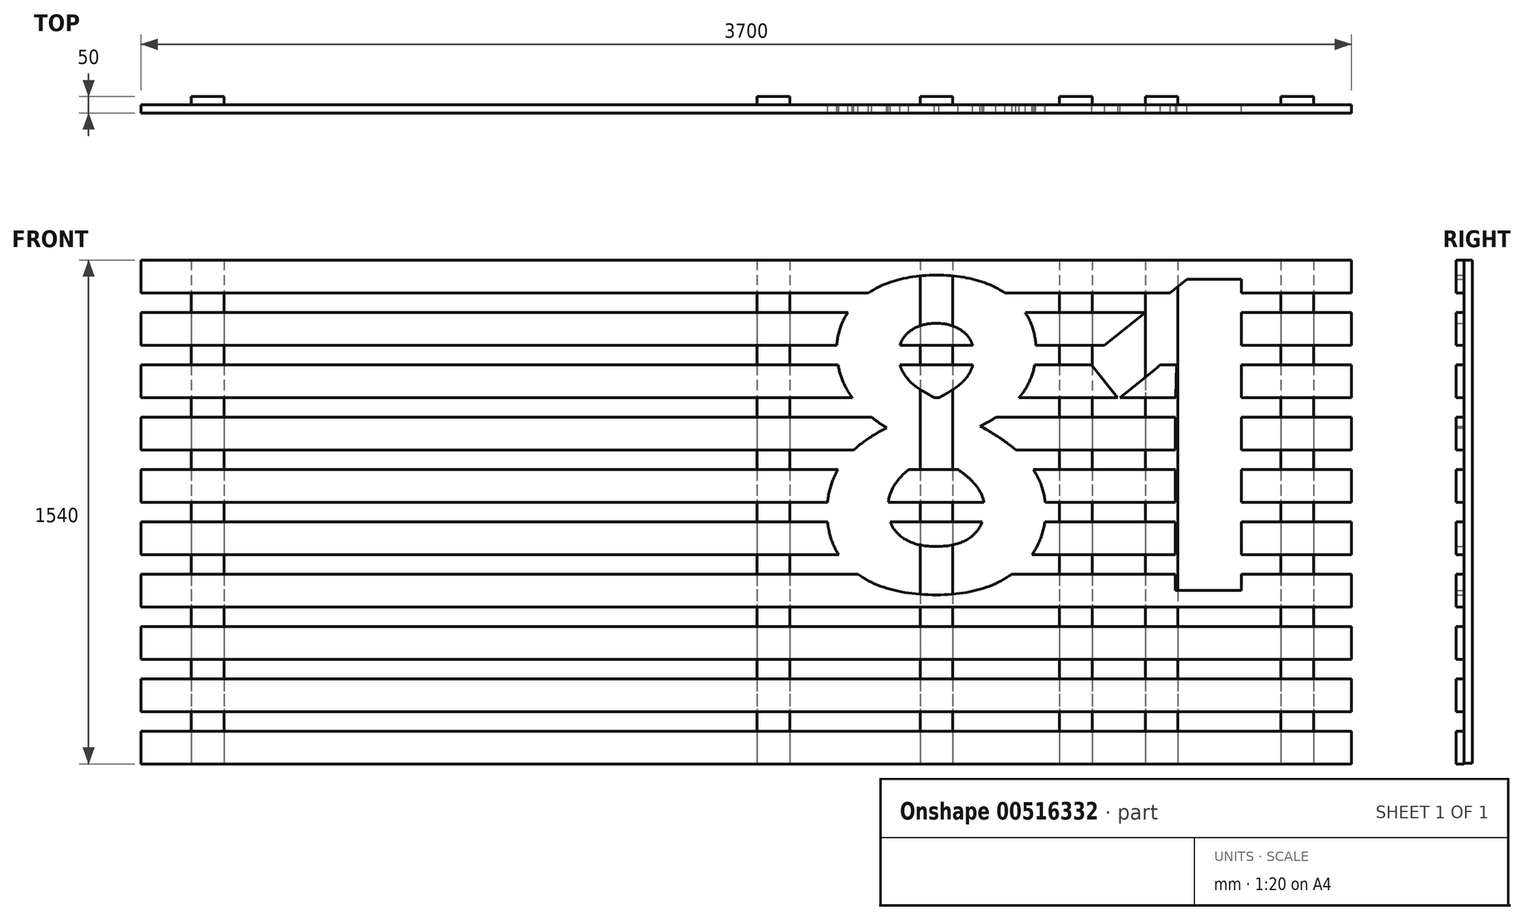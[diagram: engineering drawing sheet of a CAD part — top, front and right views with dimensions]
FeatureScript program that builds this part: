
annotation { "Feature Type Name" : "Feature", "Feature Type Description" : "" }
export const myFeature = defineFeature(function(context is Context, id is Id, definition is map)
    precondition{}
    {
        {
            var Q0;
            Q0=qCreatedBy(makeId("Front.planeOp"),FACE);
            var sketch = newSketch(context, id + "F0", { "sketchPlane" : qUnion([Q0])});
            skLineSegment(sketch, "E0.bottom", {"start": v(-1471.72, 851.39) * mm, "end": v(2278.28, 851.39) * mm, "construction": true});
            skLineSegment(sketch, "E0.top", {"start": v(-1471.72, -868.61) * mm, "end": v(2278.28, -868.61) * mm, "construction": true});
            skLineSegment(sketch, "E0.left", {"start": v(-1471.72, 851.39) * mm, "end": v(-1471.72, -868.61) * mm, "construction": true});
            skLineSegment(sketch, "E0.right", {"start": v(2278.28, 851.39) * mm, "end": v(2278.28, -868.61) * mm, "construction": true});
            skLineSegment(sketch, "E1.bottom", {"start": v(-1440.67, 798.6) * mm, "end": v(2259.33, 798.6) * mm});
            skLineSegment(sketch, "E1.top", {"start": v(-1440.67, 698.6) * mm, "end": v(2259.33, 698.6) * mm});
            skLineSegment(sketch, "E1.left", {"start": v(-1440.67, 798.6) * mm, "end": v(-1440.67, 698.6) * mm});
            skLineSegment(sketch, "E1.right", {"start": v(2259.33, 798.6) * mm, "end": v(2259.33, 698.6) * mm});
            skLineSegment(sketch, "E2.0.1.0", {"start": v(-1440.67, 538.6) * mm, "end": v(2259.33, 538.6) * mm});
            skLineSegment(sketch, "E2.0.1.1", {"start": v(-1440.67, 638.6) * mm, "end": v(2259.33, 638.6) * mm});
            skLineSegment(sketch, "E2.0.1.2", {"start": v(-1440.67, 638.6) * mm, "end": v(-1440.67, 538.6) * mm});
            skLineSegment(sketch, "E2.0.1.3", {"start": v(2259.33, 638.6) * mm, "end": v(2259.33, 538.6) * mm});
            skLineSegment(sketch, "E2.0.2.0", {"start": v(-1440.67, 378.6) * mm, "end": v(2259.33, 378.6) * mm});
            skLineSegment(sketch, "E2.0.2.1", {"start": v(-1440.67, 478.6) * mm, "end": v(2259.33, 478.6) * mm});
            skLineSegment(sketch, "E2.0.2.2", {"start": v(-1440.67, 478.6) * mm, "end": v(-1440.67, 378.6) * mm});
            skLineSegment(sketch, "E2.0.2.3", {"start": v(2259.33, 478.6) * mm, "end": v(2259.33, 378.6) * mm});
            skLineSegment(sketch, "E2.0.3.0", {"start": v(-1440.67, 218.6) * mm, "end": v(2259.33, 218.6) * mm});
            skLineSegment(sketch, "E2.0.3.1", {"start": v(-1440.67, 318.6) * mm, "end": v(2259.33, 318.6) * mm});
            skLineSegment(sketch, "E2.0.3.2", {"start": v(-1440.67, 318.6) * mm, "end": v(-1440.67, 218.6) * mm});
            skLineSegment(sketch, "E2.0.3.3", {"start": v(2259.33, 318.6) * mm, "end": v(2259.33, 218.6) * mm});
            skLineSegment(sketch, "E2.0.4.0", {"start": v(-1440.67, 58.6) * mm, "end": v(2259.33, 58.6) * mm});
            skLineSegment(sketch, "E2.0.4.1", {"start": v(-1440.67, 158.6) * mm, "end": v(2259.33, 158.6) * mm});
            skLineSegment(sketch, "E2.0.4.2", {"start": v(-1440.67, 158.6) * mm, "end": v(-1440.67, 58.6) * mm});
            skLineSegment(sketch, "E2.0.4.3", {"start": v(2259.33, 158.6) * mm, "end": v(2259.33, 58.6) * mm});
            skLineSegment(sketch, "E2.0.5.0", {"start": v(-1440.67, -101.4) * mm, "end": v(2259.33, -101.4) * mm});
            skLineSegment(sketch, "E2.0.5.1", {"start": v(-1440.67, -1.4) * mm, "end": v(2259.33, -1.4) * mm});
            skLineSegment(sketch, "E2.0.5.2", {"start": v(-1440.67, -1.4) * mm, "end": v(-1440.67, -101.4) * mm});
            skLineSegment(sketch, "E2.0.5.3", {"start": v(2259.33, -1.4) * mm, "end": v(2259.33, -101.4) * mm});
            skLineSegment(sketch, "E2.0.6.0", {"start": v(-1440.67, -261.4) * mm, "end": v(2259.33, -261.4) * mm});
            skLineSegment(sketch, "E2.0.6.1", {"start": v(-1440.67, -161.4) * mm, "end": v(2259.33, -161.4) * mm});
            skLineSegment(sketch, "E2.0.6.2", {"start": v(-1440.67, -161.4) * mm, "end": v(-1440.67, -261.4) * mm});
            skLineSegment(sketch, "E2.0.6.3", {"start": v(2259.33, -161.4) * mm, "end": v(2259.33, -261.4) * mm});
            skLineSegment(sketch, "E2.0.7.0", {"start": v(-1440.67, -421.4) * mm, "end": v(2259.33, -421.4) * mm});
            skLineSegment(sketch, "E2.0.7.1", {"start": v(-1440.67, -321.4) * mm, "end": v(2259.33, -321.4) * mm});
            skLineSegment(sketch, "E2.0.7.2", {"start": v(-1440.67, -321.4) * mm, "end": v(-1440.67, -421.4) * mm});
            skLineSegment(sketch, "E2.0.7.3", {"start": v(2259.33, -321.4) * mm, "end": v(2259.33, -421.4) * mm});
            skLineSegment(sketch, "E2.direction1", {"start": v(-1440.67, 698.6) * mm, "end": v(-2006.52, 698.6) * mm, "construction": true});
            skLineSegment(sketch, "E2.direction2", {"start": v(-1440.67, 698.6) * mm, "end": v(-1440.67, 538.6) * mm, "construction": true});
            skLineSegment(sketch, "E3.0.0.8", {"start": v(-1440.67, -581.4) * mm, "end": v(2259.33, -581.4) * mm});
            skLineSegment(sketch, "E3.3.0.8", {"start": v(-1440.67, -481.4) * mm, "end": v(2259.33, -481.4) * mm});
            skLineSegment(sketch, "E3.6.0.8", {"start": v(-1440.67, -481.4) * mm, "end": v(-1440.67, -581.4) * mm});
            skLineSegment(sketch, "E3.9.0.8", {"start": v(2259.33, -481.4) * mm, "end": v(2259.33, -581.4) * mm});
            skLineSegment(sketch, "E3.0.0.9", {"start": v(-1440.67, -741.4) * mm, "end": v(2259.33, -741.4) * mm});
            skLineSegment(sketch, "E3.3.0.9", {"start": v(-1440.67, -641.4) * mm, "end": v(2259.33, -641.4) * mm});
            skLineSegment(sketch, "E3.6.0.9", {"start": v(-1440.67, -641.4) * mm, "end": v(-1440.67, -741.4) * mm});
            skLineSegment(sketch, "E3.9.0.9", {"start": v(2259.33, -641.4) * mm, "end": v(2259.33, -741.4) * mm});
            skSolve(sketch);
        }
        {
            var Q0;
            Q0 = qSketchRegion(id + "F0", true);
            extrude(context, id + "F1", {"entities" : qUnion([Q0]), "depth" : 25 * mm, "offsetDistance" : 25 * mm});
        }
        {
            var Q0;
            Q0=qCreatedBy(makeId("Front.planeOp"),FACE);
            var sketch = newSketch(context, id + "F2", { "sketchPlane" : qUnion([Q0])});
            skText(sketch, "E4", { "text": "81", "fontName": "NotoSans-Bold.ttf"});
            skLineSegment(sketch, "E5", {"start": v(5049.15, 398.6) * mm, "end": v(5049.15, -21.4) * mm});
            skCircle(sketch, "E6", {"center": v(5049.15, 398.6) * mm, "radius": 275 * mm});
            skCircle(sketch, "E7", {"center": v(5049.15, 398.6) * mm, "radius": 140 * mm});
            skCircle(sketch, "E8", {"center": v(5049.15, -21.4) * mm, "radius": 275 * mm});
            skCircle(sketch, "E9", {"center": v(5049.15, -21.4) * mm, "radius": 140 * mm});
            skLineSegment(sketch, "E10", {"start": v(5374.15, 469.35) * mm, "end": v(5454.5, 373.6) * mm});
            skLineSegment(sketch, "E11", {"start": v(5454.5, 373.6) * mm, "end": v(5594.15, 490.78) * mm});
            skLineSegment(sketch, "E12", {"start": v(5594.15, 490.78) * mm, "end": v(5594.15, -296.4) * mm});
            skLineSegment(sketch, "E13", {"start": v(5594.15, -296.4) * mm, "end": v(5774.15, -296.4) * mm});
            skLineSegment(sketch, "E14", {"start": v(5774.15, -296.4) * mm, "end": v(5774.15, 673.6) * mm});
            skLineSegment(sketch, "E15", {"start": v(5617.56, 673.6) * mm, "end": v(5374.15, 469.35) * mm});
            skLineSegment(sketch, "E16", {"start": v(5617.56, 673.6) * mm, "end": v(5774.15, 673.6) * mm});
            const initialGuessF2  = {"E4": [0.60975, -0.2114, 1, 0, 0.96]};
            skSetInitialGuess(sketch, initialGuessF2);
            skSolve(sketch);
        }
        {
            var Q0;
            Q0 = qSketchRegion(id + "F2", true);
            extrude(context, id + "F3", {"entities" : qUnion([Q0]), "operationType" : NewBodyOperationType.REMOVE, "endBound" : BoundingType.THROUGH_ALL, "depth" : 25 * mm, "offsetDistance" : 25 * mm});
        }
        {
            var Q0;
            Q0=qCreatedBy(makeId("Front.planeOp"),FACE);
            var sketch = newSketch(context, id + "F4", { "sketchPlane" : qUnion([Q0])});
            skLineSegment(sketch, "E17.bottom", {"start": v(442.54, 798.6) * mm, "end": v(542.54, 798.6) * mm});
            skLineSegment(sketch, "E17.top", {"start": v(442.54, -738.97) * mm, "end": v(542.54, -738.97) * mm});
            skLineSegment(sketch, "E17.left", {"start": v(442.54, 798.6) * mm, "end": v(442.54, -738.97) * mm});
            skLineSegment(sketch, "E17.right", {"start": v(542.54, 798.6) * mm, "end": v(542.54, -738.97) * mm});
            skLineSegment(sketch, "E18.bottom", {"start": v(940.94, 798.6) * mm, "end": v(1040.94, 798.6) * mm});
            skLineSegment(sketch, "E18.top", {"start": v(940.94, -738.97) * mm, "end": v(1040.94, -738.97) * mm});
            skLineSegment(sketch, "E18.left", {"start": v(940.94, 798.6) * mm, "end": v(940.94, -738.97) * mm});
            skLineSegment(sketch, "E18.right", {"start": v(1040.94, 798.6) * mm, "end": v(1040.94, -738.97) * mm});
            skLineSegment(sketch, "E19.bottom", {"start": v(-1286.87, 798.6) * mm, "end": v(-1186.87, 798.6) * mm});
            skLineSegment(sketch, "E19.top", {"start": v(-1286.87, -738.97) * mm, "end": v(-1186.87, -738.97) * mm});
            skLineSegment(sketch, "E19.left", {"start": v(-1286.87, 798.6) * mm, "end": v(-1286.87, -738.97) * mm});
            skLineSegment(sketch, "E19.right", {"start": v(-1186.87, 798.6) * mm, "end": v(-1186.87, -738.97) * mm});
            skLineSegment(sketch, "E20.bottom", {"start": v(1629.24, 798.6) * mm, "end": v(1729.24, 798.6) * mm});
            skLineSegment(sketch, "E20.top", {"start": v(1629.24, -738.97) * mm, "end": v(1729.24, -738.97) * mm});
            skLineSegment(sketch, "E20.left", {"start": v(1629.24, 798.6) * mm, "end": v(1629.24, -738.97) * mm});
            skLineSegment(sketch, "E20.right", {"start": v(1729.24, 798.6) * mm, "end": v(1729.24, -738.97) * mm});
            skLineSegment(sketch, "E21.bottom", {"start": v(1366.73, 798.6) * mm, "end": v(1466.73, 798.6) * mm});
            skLineSegment(sketch, "E21.top", {"start": v(1366.73, -738.97) * mm, "end": v(1466.73, -738.97) * mm});
            skLineSegment(sketch, "E21.left", {"start": v(1366.73, 798.6) * mm, "end": v(1366.73, -738.97) * mm});
            skLineSegment(sketch, "E21.right", {"start": v(1466.73, 798.6) * mm, "end": v(1466.73, -738.97) * mm});
            skLineSegment(sketch, "E22.bottom", {"start": v(2043.95, 798.6) * mm, "end": v(2143.95, 798.6) * mm});
            skLineSegment(sketch, "E22.top", {"start": v(2043.95, -738.97) * mm, "end": v(2143.95, -738.97) * mm});
            skLineSegment(sketch, "E22.left", {"start": v(2043.95, 798.6) * mm, "end": v(2043.95, -738.97) * mm});
            skLineSegment(sketch, "E22.right", {"start": v(2143.95, 798.6) * mm, "end": v(2143.95, -738.97) * mm});
            skSolve(sketch);
        }
        {
            var Q0;
            Q0 = qSketchRegion(id + "F4", true);
            extrude(context, id + "F5", {"entities" : qUnion([Q0]), "oppositeDirection" : true, "depth" : 25 * mm, "offsetDistance" : 25 * mm});
        }
    });
